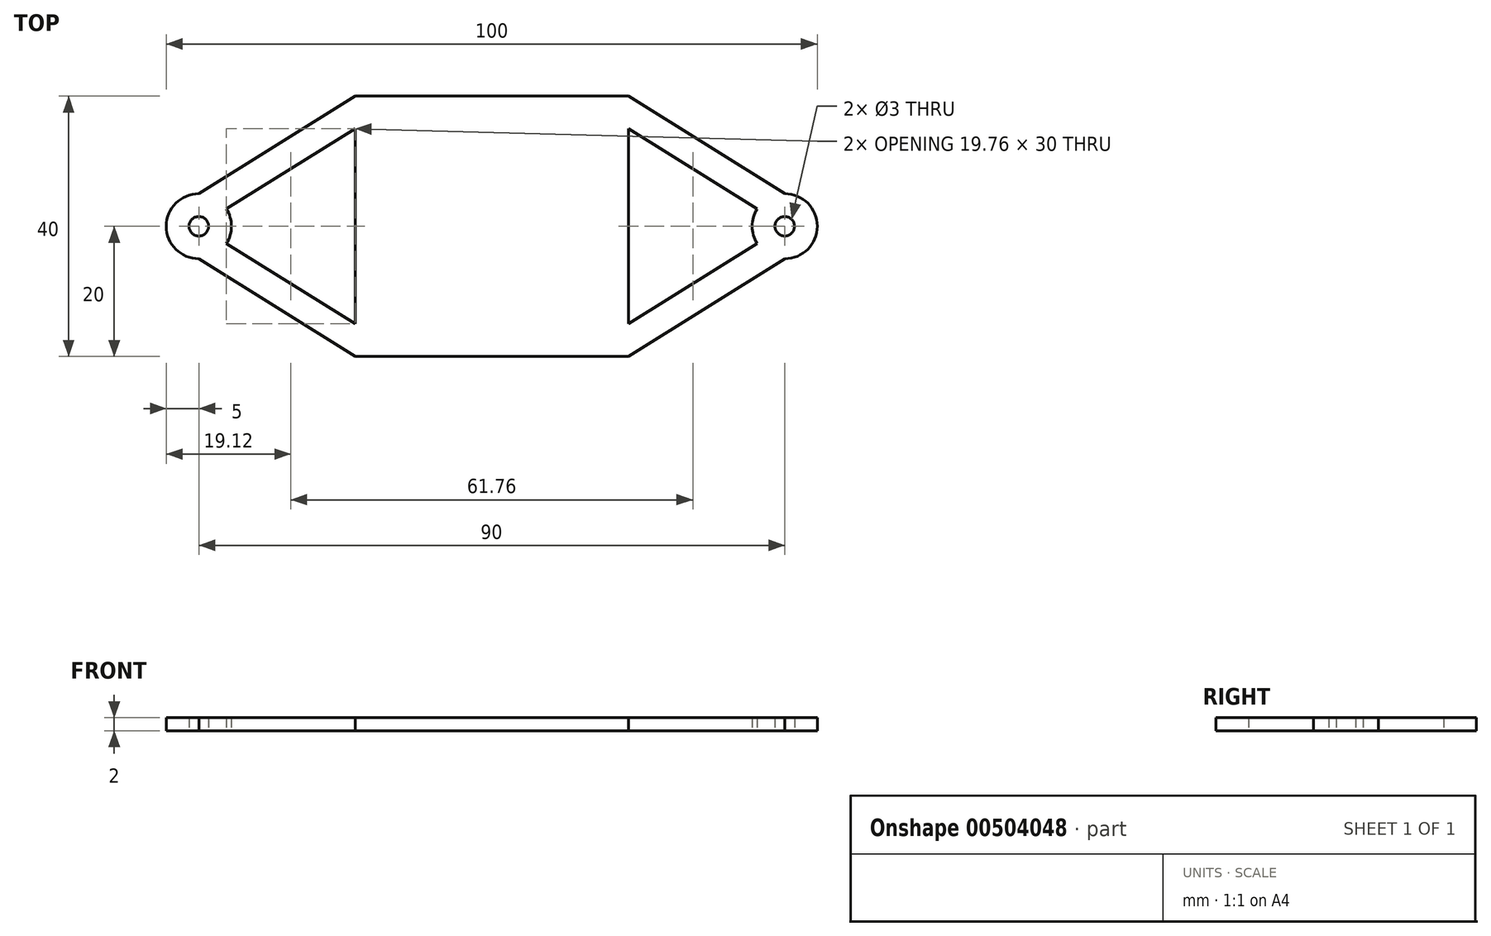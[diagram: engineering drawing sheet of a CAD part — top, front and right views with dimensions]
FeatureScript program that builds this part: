
annotation { "Feature Type Name" : "Feature", "Feature Type Description" : "" }
export const myFeature = defineFeature(function(context is Context, id is Id, definition is map)
    precondition{}
    {
        {
            var Q0;
            Q0=qCreatedBy(makeId("Top.planeOp"),FACE);
            var sketch = newSketch(context, id + "F0", { "sketchPlane" : qUnion([Q0])});
            skCircle(sketch, "E0", {"center": v(-45, 0) * mm, "radius": 1.5 * mm});
            skCircle(sketch, "E1", {"center": v(-45, 0) * mm, "radius": 5 * mm});
            skCircle(sketch, "E2", {"center": v(45, 0) * mm, "radius": 1.5 * mm});
            skCircle(sketch, "E3", {"center": v(45, 0) * mm, "radius": 5 * mm});
            skLineSegment(sketch, "E4", {"start": v(-45, 0) * mm, "end": v(-45, -9.72) * mm});
            skLineSegment(sketch, "E5", {"start": v(-45, -9.72) * mm, "end": v(-45, 0) * mm});
            skLineSegment(sketch, "E6", {"start": v(-45, 0) * mm, "end": v(-45, 10.23) * mm});
            skLineSegment(sketch, "E7", {"start": v(45, 0) * mm, "end": v(45, 8.6) * mm});
            skLineSegment(sketch, "E8", {"start": v(45, 8.6) * mm, "end": v(45, 0) * mm});
            skLineSegment(sketch, "E9", {"start": v(45, 0) * mm, "end": v(45, -7.93) * mm});
            skLineSegment(sketch, "E10.bottom", {"start": v(-21, 20) * mm, "end": v(21, 20) * mm});
            skLineSegment(sketch, "E10.top", {"start": v(-21, -50) * mm, "end": v(21, -50) * mm});
            skLineSegment(sketch, "E10.left", {"start": v(-21, 20) * mm, "end": v(-21, -50) * mm});
            skLineSegment(sketch, "E10.right", {"start": v(21, 20) * mm, "end": v(21, -50) * mm});
            skLineSegment(sketch, "E11", {"start": v(-45, 0) * mm, "end": v(45, 0) * mm});
            skPoint(sketch, "E12", {"position": v(-21, -20) * mm});
            skPoint(sketch, "E13", {"position": v(21, -20) * mm});
            skLineSegment(sketch, "E14", {"start": v(-45, -5) * mm, "end": v(-21, -20) * mm});
            skLineSegment(sketch, "E15", {"start": v(-45, 5) * mm, "end": v(-21, 20) * mm});
            skLineSegment(sketch, "E16", {"start": v(21, 20) * mm, "end": v(45, 5) * mm});
            skLineSegment(sketch, "E17", {"start": v(21, -20) * mm, "end": v(45, -5) * mm});
            skPoint(sketch, "E18", {"position": v(-21, 15) * mm});
            skPoint(sketch, "E19", {"position": v(-21, -15) * mm});
            skPoint(sketch, "E20", {"position": v(21, -15) * mm});
            skPoint(sketch, "E21", {"position": v(21, 15) * mm});
            skLineSegment(sketch, "E22", {"start": v(-45, 0) * mm, "end": v(-21, 15) * mm});
            skLineSegment(sketch, "E23", {"start": v(-45, 0) * mm, "end": v(-21, -15) * mm});
            skLineSegment(sketch, "E24", {"start": v(21, 15) * mm, "end": v(45, 0) * mm});
            skLineSegment(sketch, "E25", {"start": v(21, -15) * mm, "end": v(45, 0) * mm});
            skLineSegment(sketch, "E26", {"start": v(-21, -20) * mm, "end": v(21, -20) * mm});
            skLineSegment(sketch, "E27", {"start": v(21, -15) * mm, "end": v(-21, -15) * mm});
            skLineSegment(sketch, "E28", {"start": v(-21, 15) * mm, "end": v(21, 15) * mm});
            skLineSegment(sketch, "E29", {"start": v(-15, 20) * mm, "end": v(-15, 15) * mm});
            skLineSegment(sketch, "E30", {"start": v(15, 15) * mm, "end": v(15, 20) * mm});
            skLineSegment(sketch, "E31", {"start": v(-15, -15) * mm, "end": v(-15, -20) * mm});
            skLineSegment(sketch, "E32", {"start": v(15, -15) * mm, "end": v(15, -20) * mm});
            skSolve(sketch);
        }
        {
            var Q0;
            {var subQ0=sQuery(id+"F0.wireOp",EDGE,"E6");var subQ1=sQuery(id+"F0.wireOp",EDGE,"E0");var subQ2=makeQuery(id+"F0.imprint","INTERSECT",VERTEX,{"derivedFrom":[subQ1,subQ0]});Q0=makeQuery(id+"F0.imprint","IMPRINT",FACE,{"disambiguationData":[TD([[makeQuery(id+"F0.imprint","IMPRINT",EDGE,{"disambiguationData":[TD([[subQ2,-1.0]])],"derivedFrom":subQ1}),-1.0]])]});}
            var Q1;
            {var subQ0=sQuery(id+"F0.wireOp",EDGE,"E15");Q1=makeQuery(id+"F0.imprint","IMPRINT",FACE,{"disambiguationData":[TD([[makeQuery(id+"F0.imprint","IMPRINT",EDGE,{"derivedFrom":subQ0}),-1.0]])]});}
            var Q2;
            {var subQ0=sQuery(id+"F0.wireOp",EDGE,"E14");Q2=makeQuery(id+"F0.imprint","IMPRINT",FACE,{"disambiguationData":[TD([[makeQuery(id+"F0.imprint","IMPRINT",EDGE,{"derivedFrom":subQ0}),1.0]])]});}
            var Q3;
            {var subQ0=sQuery(id+"F0.wireOp",EDGE,"E8");var subQ1=sQuery(id+"F0.wireOp",EDGE,"E2");var subQ2=makeQuery(id+"F0.imprint","INTERSECT",VERTEX,{"derivedFrom":[subQ1,subQ0]});Q3=makeQuery(id+"F0.imprint","IMPRINT",FACE,{"disambiguationData":[TD([[makeQuery(id+"F0.imprint","IMPRINT",EDGE,{"disambiguationData":[TD([[subQ2,1.0]])],"derivedFrom":subQ1}),-1.0]])]});}
            var Q4;
            {var subQ0=sQuery(id+"F0.wireOp",EDGE,"E16");Q4=makeQuery(id+"F0.imprint","IMPRINT",FACE,{"disambiguationData":[TD([[makeQuery(id+"F0.imprint","IMPRINT",EDGE,{"derivedFrom":subQ0}),-1.0]])]});}
            var Q5;
            {var subQ0=sQuery(id+"F0.wireOp",EDGE,"E17");Q5=makeQuery(id+"F0.imprint","IMPRINT",FACE,{"disambiguationData":[TD([[makeQuery(id+"F0.imprint","IMPRINT",EDGE,{"derivedFrom":subQ0}),1.0]])]});}
            var Q6;
            {var subQ3=sQuery(id+"F0.wireOp",EDGE,"E29");Q6=makeQuery(id+"F0.imprint","IMPRINT",FACE,{"disambiguationData":[TD([[makeQuery(id+"F0.imprint","IMPRINT",EDGE,{"derivedFrom":subQ3}),-1.0]])]});}
            var Q7;
            {var subQ0=sQuery(id+"F0.wireOp",EDGE,"E29");Q7=makeQuery(id+"F0.imprint","IMPRINT",FACE,{"disambiguationData":[TD([[makeQuery(id+"F0.imprint","IMPRINT",EDGE,{"derivedFrom":subQ0}),1.0]])]});}
            var Q8;
            {var subQ3=sQuery(id+"F0.wireOp",EDGE,"E30");Q8=makeQuery(id+"F0.imprint","IMPRINT",FACE,{"disambiguationData":[TD([[makeQuery(id+"F0.imprint","IMPRINT",EDGE,{"derivedFrom":subQ3}),-1.0]])]});}
            var Q9;
            {var subQ0=sQuery(id+"F0.wireOp",EDGE,"E22");var subQ1=sQuery(id+"F0.wireOp",EDGE,"E0");var subQ2=makeQuery(id+"F0.imprint","INTERSECT",VERTEX,{"derivedFrom":[subQ1,subQ0]});Q9=makeQuery(id+"F0.imprint","IMPRINT",FACE,{"disambiguationData":[TD([[makeQuery(id+"F0.imprint","IMPRINT",EDGE,{"disambiguationData":[TD([[subQ2,-1.0]])],"derivedFrom":subQ1}),-1.0]])]});}
            var Q10;
            {var subQ0=sQuery(id+"F0.wireOp",EDGE,"E5");var subQ1=sQuery(id+"F0.wireOp",EDGE,"E0");var subQ2=makeQuery(id+"F0.imprint","INTERSECT",VERTEX,{"derivedFrom":[subQ1,subQ0]});Q10=makeQuery(id+"F0.imprint","IMPRINT",FACE,{"disambiguationData":[TD([[makeQuery(id+"F0.imprint","IMPRINT",EDGE,{"disambiguationData":[TD([[subQ2,-1.0]])],"derivedFrom":subQ1}),-1.0]])]});}
            var Q11;
            {var subQ0=sQuery(id+"F0.wireOp",EDGE,"E24");var subQ1=sQuery(id+"F0.wireOp",EDGE,"E2");var subQ2=makeQuery(id+"F0.imprint","INTERSECT",VERTEX,{"derivedFrom":[subQ1,subQ0]});Q11=makeQuery(id+"F0.imprint","IMPRINT",FACE,{"disambiguationData":[TD([[makeQuery(id+"F0.imprint","IMPRINT",EDGE,{"disambiguationData":[TD([[subQ2,1.0]])],"derivedFrom":subQ1}),-1.0]])]});}
            var Q12;
            {var subQ0=sQuery(id+"F0.wireOp",EDGE,"E25");var subQ1=sQuery(id+"F0.wireOp",EDGE,"E2");var subQ2=makeQuery(id+"F0.imprint","INTERSECT",VERTEX,{"derivedFrom":[subQ1,subQ0]});Q12=makeQuery(id+"F0.imprint","IMPRINT",FACE,{"disambiguationData":[TD([[makeQuery(id+"F0.imprint","IMPRINT",EDGE,{"disambiguationData":[TD([[subQ2,-1.0]])],"derivedFrom":subQ1}),-1.0]])]});}
            var Q13;
            {var subQ5=sQuery(id+"F0.wireOp",EDGE,"E31");Q13=makeQuery(id+"F0.imprint","IMPRINT",FACE,{"disambiguationData":[TD([[makeQuery(id+"F0.imprint","IMPRINT",EDGE,{"derivedFrom":subQ5}),-1.0]])]});}
            var Q14;
            {var subQ5=sQuery(id+"F0.wireOp",EDGE,"E32");Q14=makeQuery(id+"F0.imprint","IMPRINT",FACE,{"disambiguationData":[TD([[makeQuery(id+"F0.imprint","IMPRINT",EDGE,{"derivedFrom":subQ5}),1.0]])]});}
            var Q15;
            {var subQ0=sQuery(id+"F0.wireOp",EDGE,"E22");var subQ1=sQuery(id+"F0.wireOp",EDGE,"E0");var subQ2=makeQuery(id+"F0.imprint","INTERSECT",VERTEX,{"derivedFrom":[subQ1,subQ0]});Q15=makeQuery(id+"F0.imprint","IMPRINT",FACE,{"disambiguationData":[TD([[makeQuery(id+"F0.imprint","IMPRINT",EDGE,{"disambiguationData":[TD([[subQ2,1.0]])],"derivedFrom":subQ1}),-1.0]])]});}
            var Q16;
            {var subQ0=sQuery(id+"F0.wireOp",EDGE,"E11");var subQ1=sQuery(id+"F0.wireOp",EDGE,"E0");var subQ2=makeQuery(id+"F0.imprint","INTERSECT",VERTEX,{"derivedFrom":[subQ1,subQ0]});Q16=makeQuery(id+"F0.imprint","IMPRINT",FACE,{"disambiguationData":[TD([[makeQuery(id+"F0.imprint","IMPRINT",EDGE,{"disambiguationData":[TD([[subQ2,1.0]])],"derivedFrom":subQ1}),-1.0]])]});}
            var Q17;
            {var subQ0=sQuery(id+"F0.wireOp",EDGE,"E24");var subQ1=sQuery(id+"F0.wireOp",EDGE,"E2");var subQ2=makeQuery(id+"F0.imprint","INTERSECT",VERTEX,{"derivedFrom":[subQ1,subQ0]});Q17=makeQuery(id+"F0.imprint","IMPRINT",FACE,{"disambiguationData":[TD([[makeQuery(id+"F0.imprint","IMPRINT",EDGE,{"disambiguationData":[TD([[subQ2,-1.0]])],"derivedFrom":subQ1}),-1.0]])]});}
            var Q18;
            {var subQ0=sQuery(id+"F0.wireOp",EDGE,"E11");var subQ1=sQuery(id+"F0.wireOp",EDGE,"E2");var subQ2=makeQuery(id+"F0.imprint","INTERSECT",VERTEX,{"derivedFrom":[subQ1,subQ0]});Q18=makeQuery(id+"F0.imprint","IMPRINT",FACE,{"disambiguationData":[TD([[makeQuery(id+"F0.imprint","IMPRINT",EDGE,{"disambiguationData":[TD([[subQ2,-1.0]])],"derivedFrom":subQ1}),-1.0]])]});}
            var Q19;
            {var subQ1=sQuery(id+"F0.wireOp",EDGE,"E10.left");var subQ6=sQuery(id+"F0.wireOp",EDGE,"E11");var subQ8=makeQuery(id+"F0.imprint","INTERSECT",VERTEX,{"derivedFrom":[subQ1,subQ6]});Q19=makeQuery(id+"F0.imprint","IMPRINT",FACE,{"disambiguationData":[TD([[makeQuery(id+"F0.imprint","IMPRINT",EDGE,{"disambiguationData":[TD([[subQ8,-1.0]])],"derivedFrom":subQ6}),1.0]])]});}
            var Q20;
            {var subQ4=sQuery(id+"F0.wireOp",EDGE,"E11");var subQ5=sQuery(id+"F0.wireOp",EDGE,"E10.left");var subQ6=makeQuery(id+"F0.imprint","INTERSECT",VERTEX,{"derivedFrom":[subQ5,subQ4]});Q20=makeQuery(id+"F0.imprint","IMPRINT",FACE,{"disambiguationData":[TD([[makeQuery(id+"F0.imprint","IMPRINT",EDGE,{"disambiguationData":[TD([[subQ6,-1.0]])],"derivedFrom":subQ4}),-1.0]])]});}
            var Q21;
            {var subQ0=sQuery(id+"F0.wireOp",EDGE,"E31");Q21=makeQuery(id+"F0.imprint","IMPRINT",FACE,{"disambiguationData":[TD([[makeQuery(id+"F0.imprint","IMPRINT",EDGE,{"derivedFrom":subQ0}),1.0]])]});}
            extrude(context, id + "F1", {"entities" : qUnion([Q0, Q1, Q2, Q3, Q4, Q5, Q6, Q7, Q8, Q9, Q10, Q11, Q12, Q13, Q14, Q15, Q16, Q17, Q18, Q19, Q20, Q21]), "depth" : 2 * mm});
        }
    });
